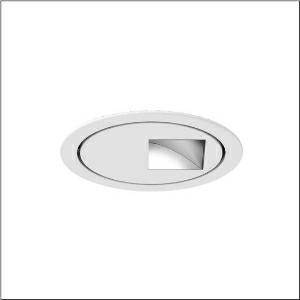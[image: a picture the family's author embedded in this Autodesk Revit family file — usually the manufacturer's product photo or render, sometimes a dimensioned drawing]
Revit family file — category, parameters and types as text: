
# Revit family: lunis_11_mini_round_51dk11cd2wf21
name_source: partatom
category: Lighting Fixtures
units: mm (PartAtom-declared; Revit-internal decimal feet)

## family parameters
Cut with Voids When Loaded = No
Host = Face
Light Source = No
Part Type = Normal
Room Calculation Point = No
Round Connector Dimension = Use Diameter
Shared = No

## types (1)
- Lunis 11 mini round (1 x LED 3000K / CRI = 80 (unbekannt), 2380 lm, 3000K)
    Apparent Load = 28 VA
    CIE Flux Codes = 44 77 97 100 100
    Color Rendering = 80
    Color Temperature = 3000K
    Default Elevation = 1800 mm
    Description = Lunis 11 mini round, downlight, light control with wallwasher, of highly reflective aluminium, highly specular, light emission: direct distribution, LED rated luminous flux: 2.380lm, light colour: 830, control gear: ECG, with terminal, 5-pole, mains connection: 220..230V, AC/DC, 0/50..60Hz, LED module, luminaire module, of aluminium, highly specular, white, diameter: 176mm, clamping range: 1..40mm, recessing ring, of plastic, traffic white (RAL 9016), protection rating (complete): IP20, insulation class (complete): insulation class II (safety insulation), certification: CE, permissible ambient temperature for indoor applications: 0..+35°C, packaging unit: 1 piece
    Height = 0 mm  [stored 0 ft]
    Lamp = 1 x LED 3000K / CRI >= 80 (unbekannt)
    Lamp Light Flux = 2380 lm
    Lamp count = 1
    Length = 176 mm
    Luminous efficacy = 86 lm/W
    Manufacturer = Siteco
    ModVariant = No
    Model = 51DK11CD2WF21
    Mounting Place = Ceiling
    Mounting Type = Recessed
    Number of Poles = 1
    OnlyDefault = Yes
    Power Factor = 1
    Product Name = Lunis 11 mini round
    Product group = downlight | ceiling recessed
    ProductGroupID = 402
    Protection Class = Protection class II
    Protection Degree = IP 20
    RLX_Detail_Level = 1
    RlxData = <blob elided: 59417 chars, md5=db814f8c>
    Socket = socket
    Standby Power = 0 W
    System Light Flux = 2380 lm
    System Power = 28 W
    Type Comments = Product without accessories
    Type Image = l_1004772.jpg
    URL = http://relux.com
    VarID = ---
    Voltage = 0 V
    Weight = 0.00 kg
    Width = 176 mm

note: [stored X ft] marks values corroborated as IEEE doubles in the binary element streams (Revit-internal decimal feet)

## geometry (parser evidence)
native form markers: Blend x4, Sweep x12
no freeform markers — native parametric forms only
